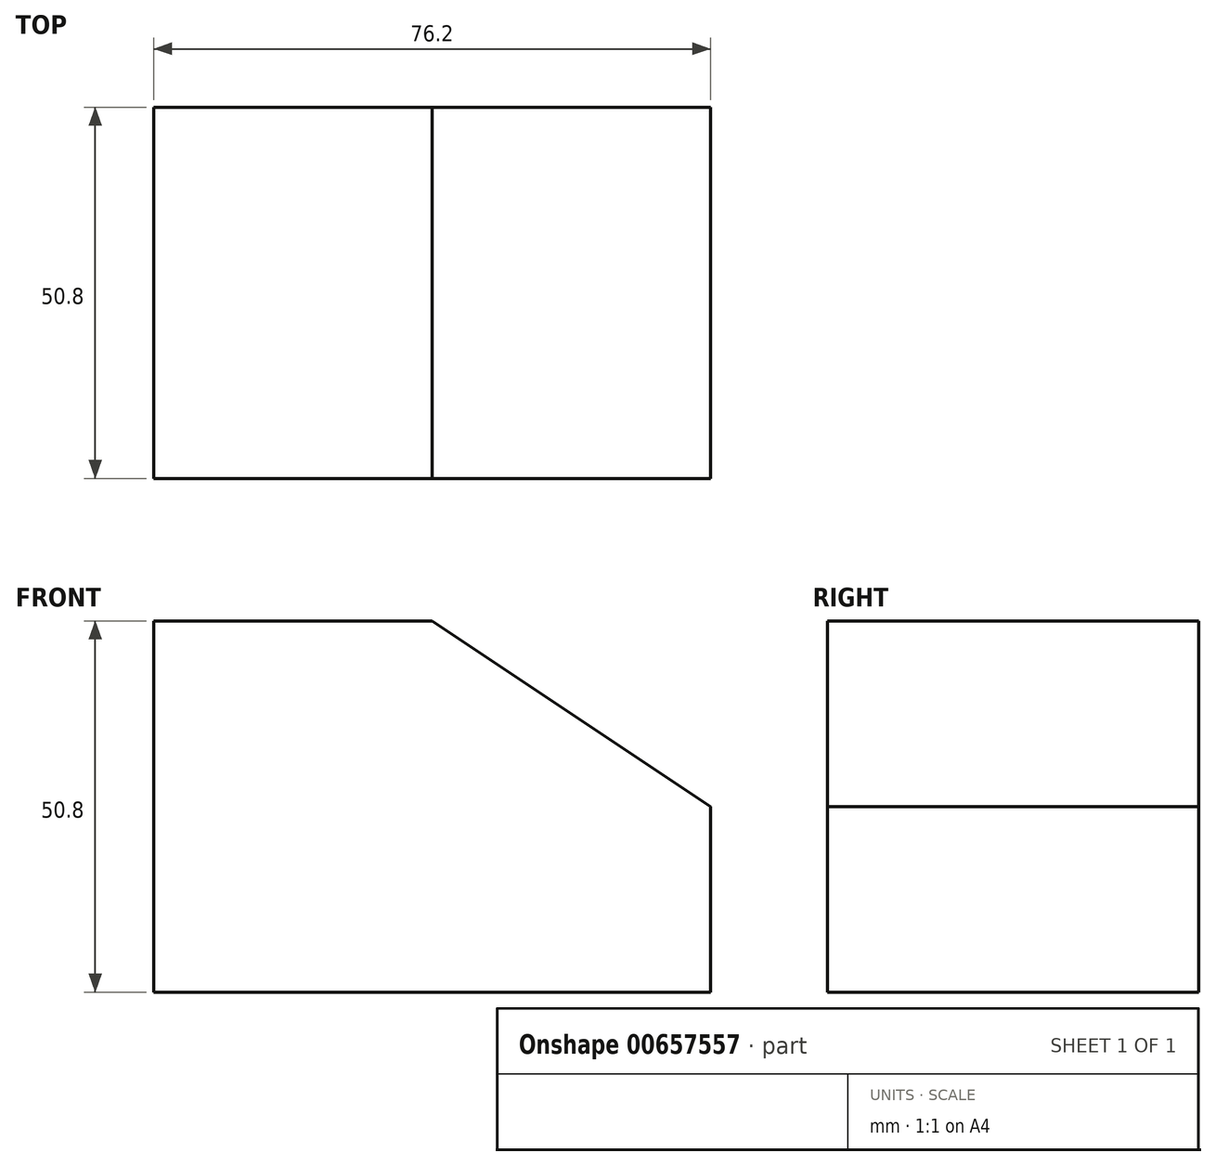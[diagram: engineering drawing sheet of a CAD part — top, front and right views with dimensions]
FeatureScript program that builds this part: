
annotation { "Feature Type Name" : "Feature", "Feature Type Description" : "" }
export const myFeature = defineFeature(function(context is Context, id is Id, definition is map)
    precondition{}
    {
        {
            var Q0;
            Q0=qCreatedBy(makeId("Front.planeOp"),FACE);
            var sketch = newSketch(context, id + "F0", { "sketchPlane" : qUnion([Q0])});
            skLineSegment(sketch, "E0", {"start": v(22.7, -44.5) * mm, "end": v(-53.5, -44.5) * mm});
            skLineSegment(sketch, "E1", {"start": v(-53.5, -44.5) * mm, "end": v(-53.5, 6.3) * mm});
            skLineSegment(sketch, "E2", {"start": v(-53.5, 6.3) * mm, "end": v(-15.4, 6.3) * mm});
            skLineSegment(sketch, "E3", {"start": v(22.7, -44.5) * mm, "end": v(22.7, -19.1) * mm});
            skPoint(sketch, "E3.endSnap0", {"position": v(-53.5, -19.1) * mm});
            skLineSegment(sketch, "E4", {"start": v(22.7, -19.1) * mm, "end": v(-15.4, 6.3) * mm});
            skSolve(sketch);
        }
        {
            var Q0;
            Q0=makeQuery(id+"F0.imprint","IMPRINT",FACE,{"disambiguationData":[TD([[makeQuery(id+"F0.imprint","IMPRINT",EDGE,{"derivedFrom":sQuery(id+"F0.wireOp",EDGE,"E0")}),-1.0]])]});
            extrude(context, id + "F1", {"entities" : qUnion([Q0]), "depth" : 50.8 * mm, "offsetDistance" : 25.4 * mm});
        }
    });
